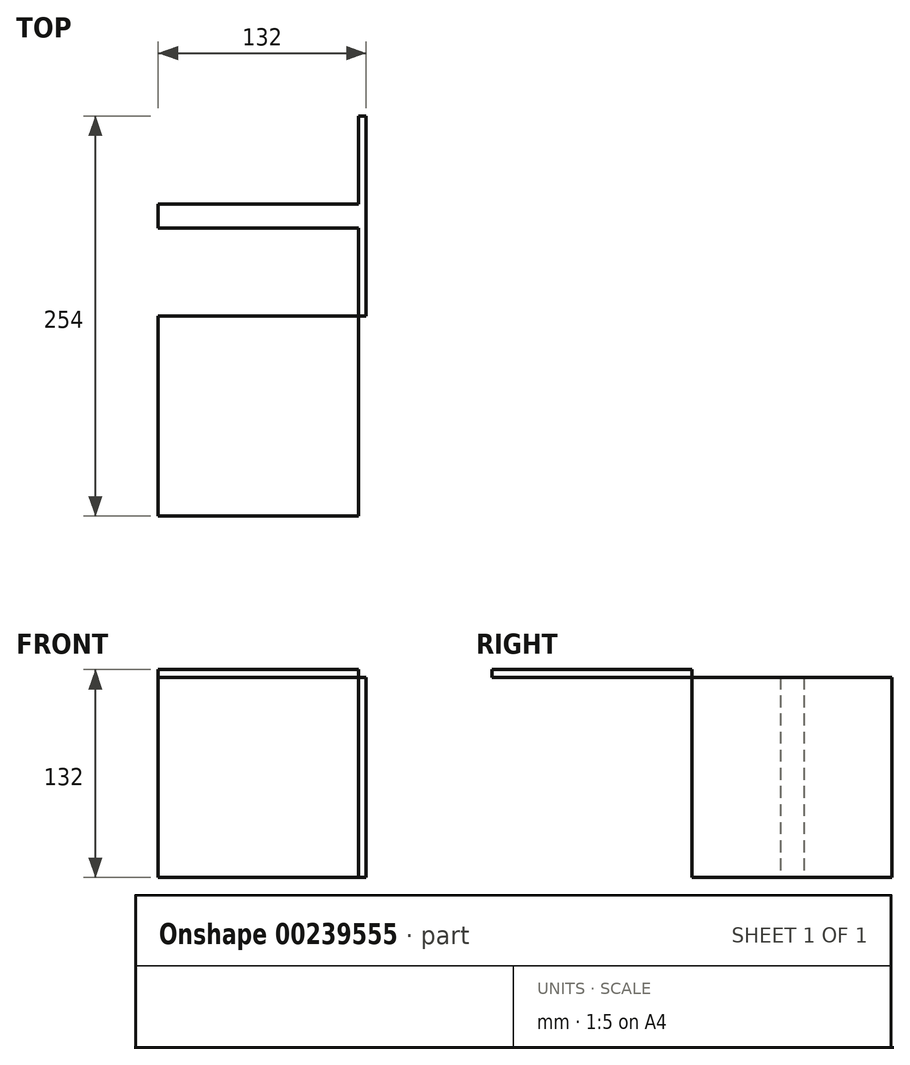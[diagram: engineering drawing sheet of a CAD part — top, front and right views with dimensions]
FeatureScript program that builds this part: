
annotation { "Feature Type Name" : "Feature", "Feature Type Description" : "" }
export const myFeature = defineFeature(function(context is Context, id is Id, definition is map)
    precondition{}
    {
        {
            assignVariable(context, id + "F0", {"name" : "L", "anyValue" : 5});
        }
        {
            var Q0;
            Q0=qCreatedBy(makeId("Front.planeOp"),FACE);
            var sketch = newSketch(context, id + "F1", { "sketchPlane" : qUnion([Q0])});
            skLineSegment(sketch, "E0.bottom", {"start": v(63.5, 63.5) * mm, "end": v(-63.5, 63.5) * mm});
            skLineSegment(sketch, "E0.top", {"start": v(63.5, -63.5) * mm, "end": v(-63.5, -63.5) * mm});
            skLineSegment(sketch, "E0.left", {"start": v(63.5, 63.5) * mm, "end": v(63.5, -63.5) * mm});
            skLineSegment(sketch, "E0.right", {"start": v(-63.5, 63.5) * mm, "end": v(-63.5, -63.5) * mm});
            skPoint(sketch, "E0.middle", {"position": v(0, 0) * mm});
            skSolve(sketch);
        }
        {
            var Q0;
            Q0 = qSketchRegion(id + "F1", true);
            extrude(context, id + "F2", {"entities" : qUnion([Q0]), "endBound" : BoundingType.SYMMETRIC, "depth" : (getVariable(context, 'L') * 3) * mm});
        }
        {
            var Q0;
            Q0=makeQuery(id+"F2.opExtrude","SWEPT_FACE",FACE,{"disambiguationData":[OSD([sQuery(id+"F1.wireOp",EDGE,"E0.bottom")])]});
            var sketch = newSketch(context, id + "F3", { "sketchPlane" : qUnion([Q0])});
            skLineSegment(sketch, "E1.bottom", {"start": v(63.5, -190.5) * mm, "end": v(-63.5, -190.5) * mm});
            skLineSegment(sketch, "E1.top", {"start": v(63.5, -63.5) * mm, "end": v(-63.5, -63.5) * mm});
            skLineSegment(sketch, "E1.left", {"start": v(63.5, -190.5) * mm, "end": v(63.5, -63.5) * mm});
            skLineSegment(sketch, "E1.right", {"start": v(-63.5, -190.5) * mm, "end": v(-63.5, -63.5) * mm});
            skSolve(sketch);
        }
        {
            var Q0;
            Q0 = qSketchRegion(id + "F3", true);
            extrude(context, id + "F4", {"entities" : qUnion([Q0]), "operationType" : NewBodyOperationType.ADD, "depth" : (getVariable(context, 'L')) * mm});
        }
        {
            var Q0;
            Q0=makeQuery(id+"F4.boolean.opBoolean","MERGE",FACE,{"derivedFrom":[makeQuery(id+"F2.opExtrude","SWEPT_FACE",FACE,{"disambiguationData":[OSD([sQuery(id+"F1.wireOp",EDGE,"E0.left")])]}),makeQuery(id+"F4.opExtrude","SWEPT_FACE",FACE,{"disambiguationData":[OSD([sQuery(id+"F3.wireOp",EDGE,"E1.left")])]})]});
            var sketch = newSketch(context, id + "F5", { "sketchPlane" : qUnion([Q0])});
            skLineSegment(sketch, "E2.bottom", {"start": v(-63.5, 63.5) * mm, "end": v(63.5, 63.5) * mm});
            skLineSegment(sketch, "E2.top", {"start": v(-63.5, -63.5) * mm, "end": v(63.5, -63.5) * mm});
            skLineSegment(sketch, "E2.left", {"start": v(-63.5, 63.5) * mm, "end": v(-63.5, -63.5) * mm});
            skLineSegment(sketch, "E2.right", {"start": v(63.5, 63.5) * mm, "end": v(63.5, -63.5) * mm});
            skSolve(sketch);
        }
        {
            var Q0;
            Q0 = qSketchRegion(id + "F5", true);
            extrude(context, id + "F6", {"entities" : qUnion([Q0]), "operationType" : NewBodyOperationType.ADD, "depth" : (getVariable(context, 'L')) * mm});
        }
    });
